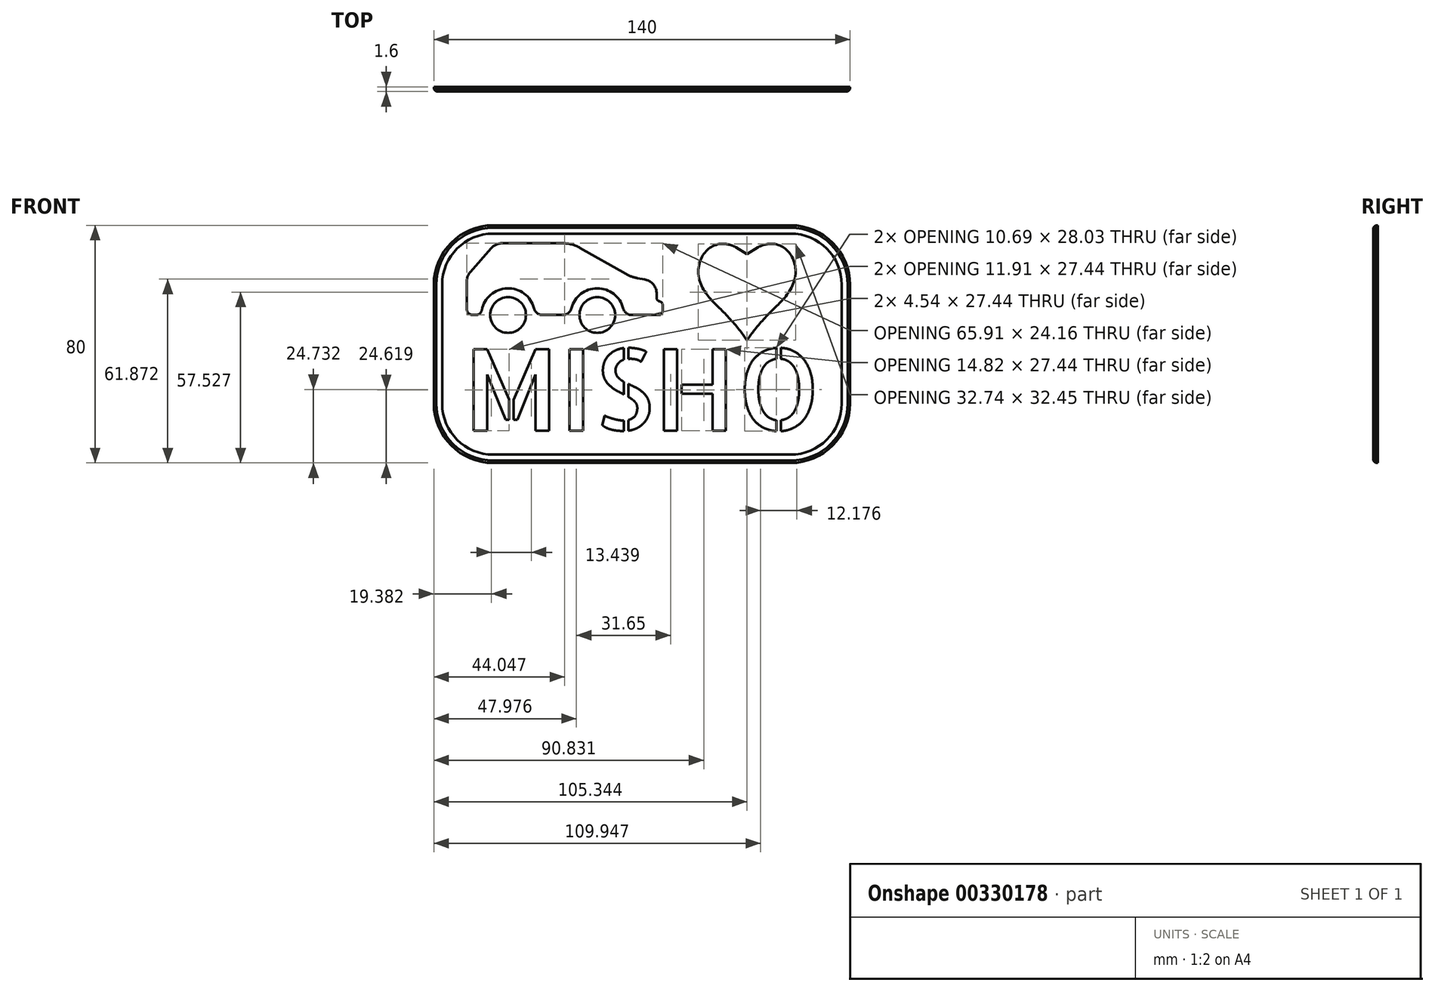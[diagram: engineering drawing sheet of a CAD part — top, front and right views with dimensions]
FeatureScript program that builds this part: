
annotation { "Feature Type Name" : "Feature", "Feature Type Description" : "" }
export const myFeature = defineFeature(function(context is Context, id is Id, definition is map)
    precondition{}
    {
        {
            var Q0;
            Q0=qCreatedBy(makeId("Front.planeOp"),FACE);
            var sketch = newSketch(context, id + "F0", { "sketchPlane" : qUnion([Q0])});
            skLineSegment(sketch, "E0.bottom", {"start": v(-70, 60) * mm, "end": v(70, 60) * mm});
            skLineSegment(sketch, "E0.top", {"start": v(-70, -20) * mm, "end": v(70, -20) * mm});
            skLineSegment(sketch, "E0.left", {"start": v(-70, 60) * mm, "end": v(-70, -20) * mm});
            skLineSegment(sketch, "E0.right", {"start": v(70, 60) * mm, "end": v(70, -20) * mm});
            skSolve(sketch);
        }
        {
            var Q0;
            Q0=qSketchRegion(id+"F0",true);
            extrude(context, id + "F1", {"entities" : qUnion([Q0]), "depth" : 1.6 * mm});
        }
        {
            var Q0;
            Q0=makeQuery(id+"F1.opExtrude","CAP_FACE",FACE,{"disambiguationData":[OSD([sQuery(id+"F0.wireOp",EDGE,"E0.bottom"),sQuery(id+"F0.wireOp",EDGE,"E0.top"),sQuery(id+"F0.wireOp",EDGE,"E0.left"),sQuery(id+"F0.wireOp",EDGE,"E0.right")])],"isStart":false});
            var sketch = newSketch(context, id + "F2", { "sketchPlane" : qUnion([Q0])});
            skText(sketch, "E1", { "text": "MISHO", "fontName": "AllertaStencil-Regular.ttf"});
            skText(sketch, "E2", { "text": "♥", "fontName": "NotoSansCJKjp-Regular.otf"});
            const initialGuessF2  = {"E1": [-0.06, -0.0091, 1, 0, 0.02745], "E2": [0.0159, 0.0228, 1, 0, 0.028]};
            skSetInitialGuess(sketch, initialGuessF2);
            skSolve(sketch);
        }
        {
            var Q0;
            Q0=qSketchRegion(id+"F2",true);
            extrude(context, id + "F3", {"entities" : qUnion([Q0]), "operationType" : NewBodyOperationType.REMOVE, "endBound" : BoundingType.THROUGH_ALL, "oppositeDirection" : true, "depth" : 25 * mm});
        }
        {
            var Q0;
            Q0=makeQuery(id+"F1.opExtrude","SWEPT_EDGE",EDGE,{"disambiguationData":[OSD([sQuery(id+"F0.wireOp",EDGE,"E0.top"),sQuery(id+"F0.wireOp",EDGE,"E0.right")])]});
            var Q1;
            Q1=makeQuery(id+"F1.opExtrude","SWEPT_EDGE",EDGE,{"disambiguationData":[OSD([sQuery(id+"F0.wireOp",EDGE,"E0.bottom"),sQuery(id+"F0.wireOp",EDGE,"E0.right")])]});
            var Q2;
            Q2=makeQuery(id+"F1.opExtrude","SWEPT_EDGE",EDGE,{"disambiguationData":[OSD([sQuery(id+"F0.wireOp",EDGE,"E0.top"),sQuery(id+"F0.wireOp",EDGE,"E0.left")])]});
            var Q3;
            Q3=makeQuery(id+"F1.opExtrude","SWEPT_EDGE",EDGE,{"disambiguationData":[OSD([sQuery(id+"F0.wireOp",EDGE,"E0.bottom"),sQuery(id+"F0.wireOp",EDGE,"E0.left")])]});
            fillet(context, id + "F4", {"entities" : qUnion([Q0, Q1, Q2, Q3]), "radius" : 20 * mm, "tangentPropagation" : true, "allowEdgeOverflow" : false});
        }
        {
            var Q0;
            Q0=makeQuery(id+"F1.opExtrude","CAP_EDGE",EDGE,{"disambiguationData":[OSD([sQuery(id+"F0.wireOp",EDGE,"E0.top")])],"isStart":false});
            chamfer(context, id + "F5", {"entities" : qUnion([Q0]), "width" : 0.8 * mm, "tangentPropagation" : true});
        }
        {
            var Q0;
            Q0=makeQuery(id+"F1.opExtrude","CAP_FACE",FACE,{"disambiguationData":[OSD([sQuery(id+"F0.wireOp",EDGE,"E0.bottom"),sQuery(id+"F0.wireOp",EDGE,"E0.top"),sQuery(id+"F0.wireOp",EDGE,"E0.left"),sQuery(id+"F0.wireOp",EDGE,"E0.right")])],"isStart":false});
            var sketch = newSketch(context, id + "F6", { "sketchPlane" : qUnion([Q0])});
            skLineSegment(sketch, "E3.0", {"start": v(-50, -17.2) * mm, "end": v(50, -17.2) * mm});
            skArc(sketch, "E3.1", {"start": v(-67.2, 0) * mm, "mid": v(-62.16, -12.16) * mm, "end": v(-50, -17.2) * mm});
            skArc(sketch, "E3.2", {"start": v(50, -17.2) * mm, "mid": v(62.16, -12.16) * mm, "end": v(67.2, 0) * mm});
            skLineSegment(sketch, "E3.3", {"start": v(-67.2, 40) * mm, "end": v(-67.2, 0) * mm});
            skLineSegment(sketch, "E3.4", {"start": v(67.2, 0) * mm, "end": v(67.2, 40) * mm});
            skArc(sketch, "E3.5", {"start": v(67.2, 40) * mm, "mid": v(62.16, 52.16) * mm, "end": v(50, 57.2) * mm});
            skLineSegment(sketch, "E3.6", {"start": v(50, 57.2) * mm, "end": v(-50, 57.2) * mm});
            skArc(sketch, "E3.7", {"start": v(-50, 57.2) * mm, "mid": v(-62.16, 52.16) * mm, "end": v(-67.2, 40) * mm});
            skSolve(sketch);
        }
        {
            var Q0;
            Q0=qSketchRegion(id+"F6",true);
            extrude(context, id + "F7", {"entities" : qUnion([Q0]), "operationType" : NewBodyOperationType.REMOVE, "oppositeDirection" : true, "depth" : 0.4 * mm});
        }
        {
            var Q0;
            Q0=makeQuery(id+"F7.boolean.opBoolean","COPY",FACE,{"derivedFrom":makeQuery(id+"F7.opExtrude","CAP_FACE",FACE,{"disambiguationData":[OSD([sQuery(id+"F6.wireOp",EDGE,"E3.0"),sQuery(id+"F6.wireOp",EDGE,"E3.1"),sQuery(id+"F6.wireOp",EDGE,"E3.2"),sQuery(id+"F6.wireOp",EDGE,"E3.3"),sQuery(id+"F6.wireOp",EDGE,"E3.4"),sQuery(id+"F6.wireOp",EDGE,"E3.5"),sQuery(id+"F6.wireOp",EDGE,"E3.6"),sQuery(id+"F6.wireOp",EDGE,"E3.7")])],"isStart":false})});
            var sketch = newSketch(context, id + "F8", { "sketchPlane" : qUnion([Q0])});
            skLineSegment(sketch, "E4", {"start": v(39.04, 52.55) * mm, "end": v(35.35, 50.27) * mm});
            skLineSegment(sketch, "E5", {"start": v(35.35, 50.27) * mm, "end": v(31.62, 52.57) * mm});
            skLineSegment(sketch, "E6", {"start": v(31.62, 52.57) * mm, "end": v(31.19, 44.7) * mm});
            skLineSegment(sketch, "E7", {"start": v(31.19, 44.7) * mm, "end": v(39.02, 44.27) * mm});
            skLineSegment(sketch, "E8", {"start": v(39.02, 44.27) * mm, "end": v(39.04, 52.55) * mm});
            skSolve(sketch);
        }
        {
            var Q0;
            Q0=qSketchRegion(id+"F8",true);
            extrude(context, id + "F9", {"entities" : qUnion([Q0]), "operationType" : NewBodyOperationType.REMOVE, "oppositeDirection" : true, "depth" : 25 * mm});
        }
        {
            var Q0;
            Q0=makeQuery(id+"F7.boolean.opBoolean","COPY",FACE,{"derivedFrom":makeQuery(id+"F7.opExtrude","CAP_FACE",FACE,{"disambiguationData":[OSD([sQuery(id+"F6.wireOp",EDGE,"E3.0"),sQuery(id+"F6.wireOp",EDGE,"E3.1"),sQuery(id+"F6.wireOp",EDGE,"E3.2"),sQuery(id+"F6.wireOp",EDGE,"E3.3"),sQuery(id+"F6.wireOp",EDGE,"E3.4"),sQuery(id+"F6.wireOp",EDGE,"E3.5"),sQuery(id+"F6.wireOp",EDGE,"E3.6"),sQuery(id+"F6.wireOp",EDGE,"E3.7")])],"isStart":false})});
            var sketch = newSketch(context, id + "F10", { "sketchPlane" : qUnion([Q0])});
            skLineSegment(sketch, "E9", {"start": v(-33.38, 29.8) * mm, "end": v(-26.62, 29.8) * mm, "construction": true});
            skCircle(sketch, "E10", {"center": v(-45, 29.8) * mm, "radius": 6 * mm});
            skCircle(sketch, "E11", {"center": v(-15, 29.8) * mm, "radius": 6 * mm});
            skArc(sketch, "E12", {"start": v(-36.29, 32.04) * mm, "mid": v(-45.31, 38.79) * mm, "end": v(-53.85, 31.43) * mm});
            skArc(sketch, "E13", {"start": v(-6.29, 32.04) * mm, "mid": v(-15, 38.8) * mm, "end": v(-23.71, 32.04) * mm});
            skLineSegment(sketch, "E14", {"start": v(-25, 29.8) * mm, "end": v(-35, 29.8) * mm});
            skLineSegment(sketch, "E15", {"start": v(-55.82, 29.8) * mm, "end": v(-56.9, 29.8) * mm});
            skLineSegment(sketch, "E16", {"start": v(-58.9, 31.8) * mm, "end": v(-58.9, 41.06) * mm});
            skLineSegment(sketch, "E17", {"start": v(-57.66, 44.36) * mm, "end": v(-50.74, 52.25) * mm});
            skLineSegment(sketch, "E18", {"start": v(-46.98, 53.95) * mm, "end": v(-26.7, 53.95) * mm});
            skLineSegment(sketch, "E19", {"start": v(-20.74, 52.37) * mm, "end": v(-5.44, 43.63) * mm});
            skLineSegment(sketch, "E20", {"start": v(-1.55, 42.22) * mm, "end": v(0.86, 41.8) * mm});
            skLineSegment(sketch, "E21", {"start": v(5, 36.88) * mm, "end": v(5, 35.45) * mm});
            skLineSegment(sketch, "E22", {"start": v(5.68, 34.45) * mm, "end": v(6, 34.45) * mm});
            skLineSegment(sketch, "E23", {"start": v(7, 33.13) * mm, "end": v(7, 31.11) * mm});
            skLineSegment(sketch, "E24", {"start": v(5.68, 29.8) * mm, "end": v(-3.38, 29.8) * mm});
            skPoint(sketch, "E25.visualSharp", {"position": v(-58.9, 42.95) * mm});
            skArc(sketch, "E25.filletArc", {"start": v(-57.66, 44.36) * mm, "mid": v(-58.59, 42.83) * mm, "end": v(-58.9, 41.06) * mm});
            skPoint(sketch, "E26.visualSharp", {"position": v(-49.24, 53.95) * mm});
            skArc(sketch, "E26.filletArc", {"start": v(-46.98, 53.95) * mm, "mid": v(-49.04, 53.5) * mm, "end": v(-50.74, 52.25) * mm});
            skPoint(sketch, "E27.visualSharp", {"position": v(-23.51, 53.95) * mm});
            skArc(sketch, "E27.filletArc", {"start": v(-20.74, 52.37) * mm, "mid": v(-23.62, 53.55) * mm, "end": v(-26.7, 53.95) * mm});
            skPoint(sketch, "E28.visualSharp", {"position": v(-3.62, 42.59) * mm});
            skArc(sketch, "E28.filletArc", {"start": v(-5.44, 43.63) * mm, "mid": v(-3.56, 42.76) * mm, "end": v(-1.55, 42.22) * mm});
            skPoint(sketch, "E29.visualSharp", {"position": v(5, 41.09) * mm});
            skArc(sketch, "E29.filletArc", {"start": v(5, 36.88) * mm, "mid": v(3.83, 40.1) * mm, "end": v(0.86, 41.8) * mm});
            skPoint(sketch, "E30.visualSharp", {"position": v(7, 34.45) * mm});
            skArc(sketch, "E30.filletArc", {"start": v(7, 33.13) * mm, "mid": v(6.61, 34.07) * mm, "end": v(5.68, 34.45) * mm});
            skPoint(sketch, "E31.visualSharp", {"position": v(7, 29.8) * mm});
            skArc(sketch, "E31.filletArc", {"start": v(5.68, 29.8) * mm, "mid": v(6.61, 30.18) * mm, "end": v(7, 31.11) * mm});
            skPoint(sketch, "E32.visualSharp", {"position": v(5, 34.45) * mm});
            skArc(sketch, "E32.filletArc", {"start": v(5, 35.45) * mm, "mid": v(5.3, 34.75) * mm, "end": v(6, 34.45) * mm});
            skPoint(sketch, "E33.newPointA", {"position": v(-36, 29.8) * mm});
            skPoint(sketch, "E33.newPointB", {"position": v(-54.05, 29.8) * mm});
            skArc(sketch, "E33.filletArc", {"start": v(-36.29, 32.04) * mm, "mid": v(-35.22, 30.42) * mm, "end": v(-33.38, 29.8) * mm});
            skArc(sketch, "E34.filletArc", {"start": v(-26.62, 29.8) * mm, "mid": v(-24.78, 30.42) * mm, "end": v(-23.71, 32.04) * mm});
            skPoint(sketch, "E35.visualSharp", {"position": v(-6, 29.8) * mm});
            skArc(sketch, "E35.filletArc", {"start": v(-6.29, 32.04) * mm, "mid": v(-5.22, 30.42) * mm, "end": v(-3.38, 29.8) * mm});
            skPoint(sketch, "E36.visualSharp", {"position": v(-54, 29.8) * mm});
            skArc(sketch, "E36.filletArc", {"start": v(-55.82, 29.8) * mm, "mid": v(-54.54, 30.25) * mm, "end": v(-53.85, 31.43) * mm});
            skPoint(sketch, "E37.visualSharp", {"position": v(-58.9, 29.8) * mm});
            skArc(sketch, "E37.filletArc", {"start": v(-58.9, 31.8) * mm, "mid": v(-58.32, 30.38) * mm, "end": v(-56.9, 29.8) * mm});
            skSolve(sketch);
        }
        {
            var Q0;
            Q0=qSketchRegion(id+"F10",true);
            extrude(context, id + "F11", {"entities" : qUnion([Q0]), "operationType" : NewBodyOperationType.REMOVE, "endBound" : BoundingType.THROUGH_ALL, "oppositeDirection" : true, "depth" : 25 * mm});
        }
    });
